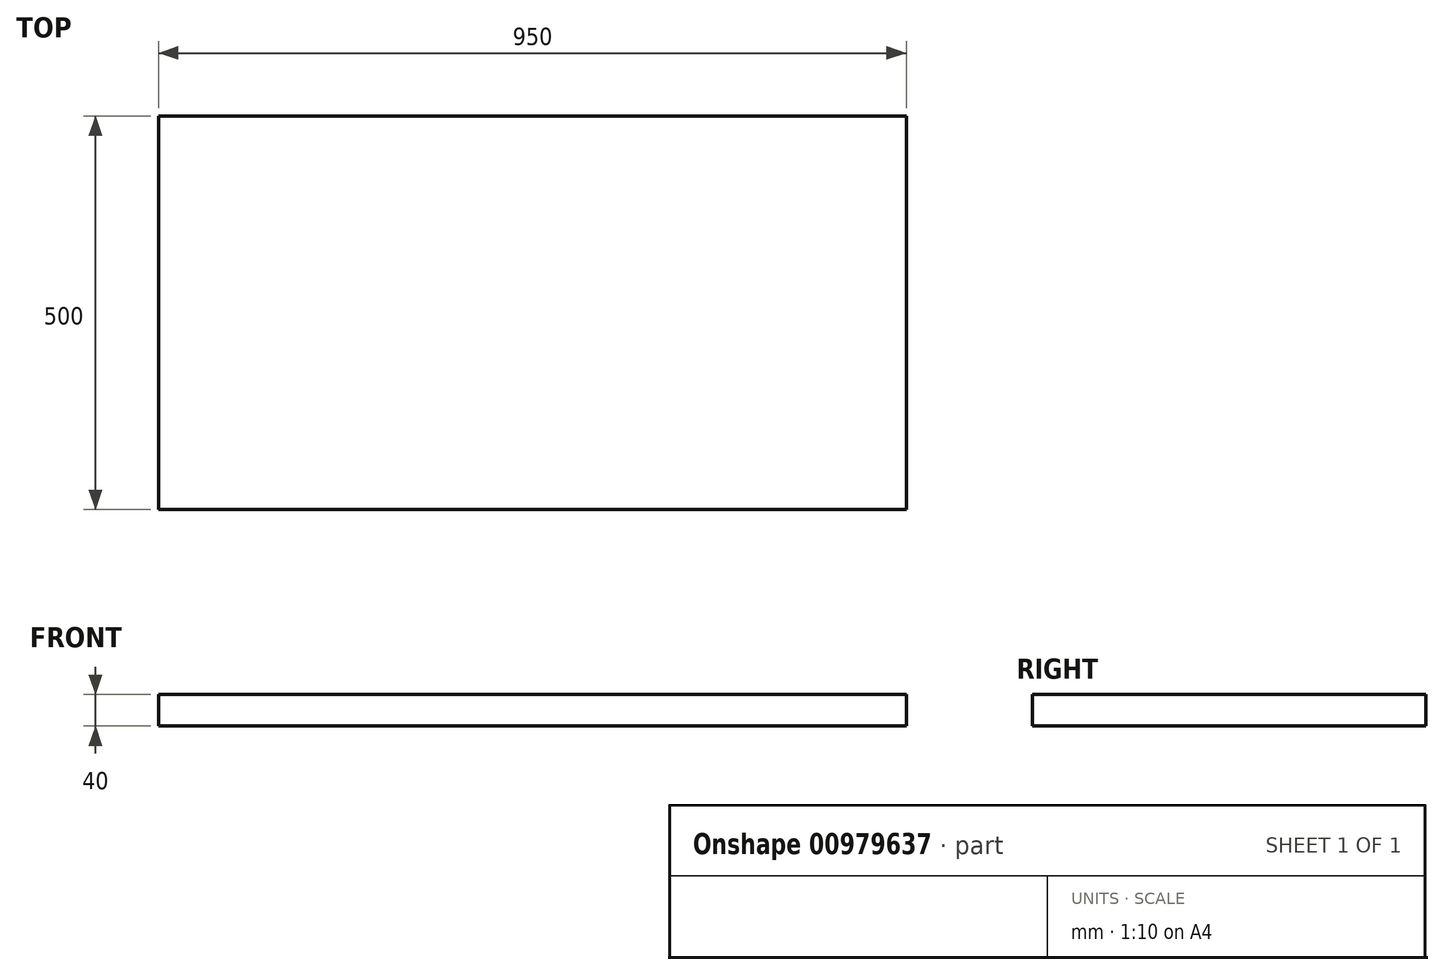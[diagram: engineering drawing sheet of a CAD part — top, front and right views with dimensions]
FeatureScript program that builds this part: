
annotation { "Feature Type Name" : "Feature", "Feature Type Description" : "" }
export const myFeature = defineFeature(function(context is Context, id is Id, definition is map)
    precondition{}
    {
        {
            var Q0;
            Q0=qCreatedBy(makeId("Top.planeOp"),FACE);
            var sketch = newSketch(context, id + "F0", { "sketchPlane" : qUnion([Q0])});
            skLineSegment(sketch, "E0.bottom", {"start": v(475, 250) * mm, "end": v(-475, 250) * mm});
            skLineSegment(sketch, "E0.top", {"start": v(475, -250) * mm, "end": v(-475, -250) * mm});
            skLineSegment(sketch, "E0.left", {"start": v(475, 250) * mm, "end": v(475, -250) * mm});
            skLineSegment(sketch, "E0.right", {"start": v(-475, 250) * mm, "end": v(-475, -250) * mm});
            skPoint(sketch, "E0.middle", {"position": v(0, 0) * mm});
            skSolve(sketch);
        }
        {
            var Q0;
            Q0=makeQuery(id+"F0.imprint","IMPRINT",FACE,{"disambiguationData":[TD([[makeQuery(id+"F0.imprint","IMPRINT",EDGE,{"derivedFrom":sQuery(id+"F0.wireOp",EDGE,"E0.bottom")}),1.0]])]});
            extrude(context, id + "F1", {"entities" : qUnion([Q0]), "depth" : 40 * mm, "offsetDistance" : 25 * mm});
        }
    });
